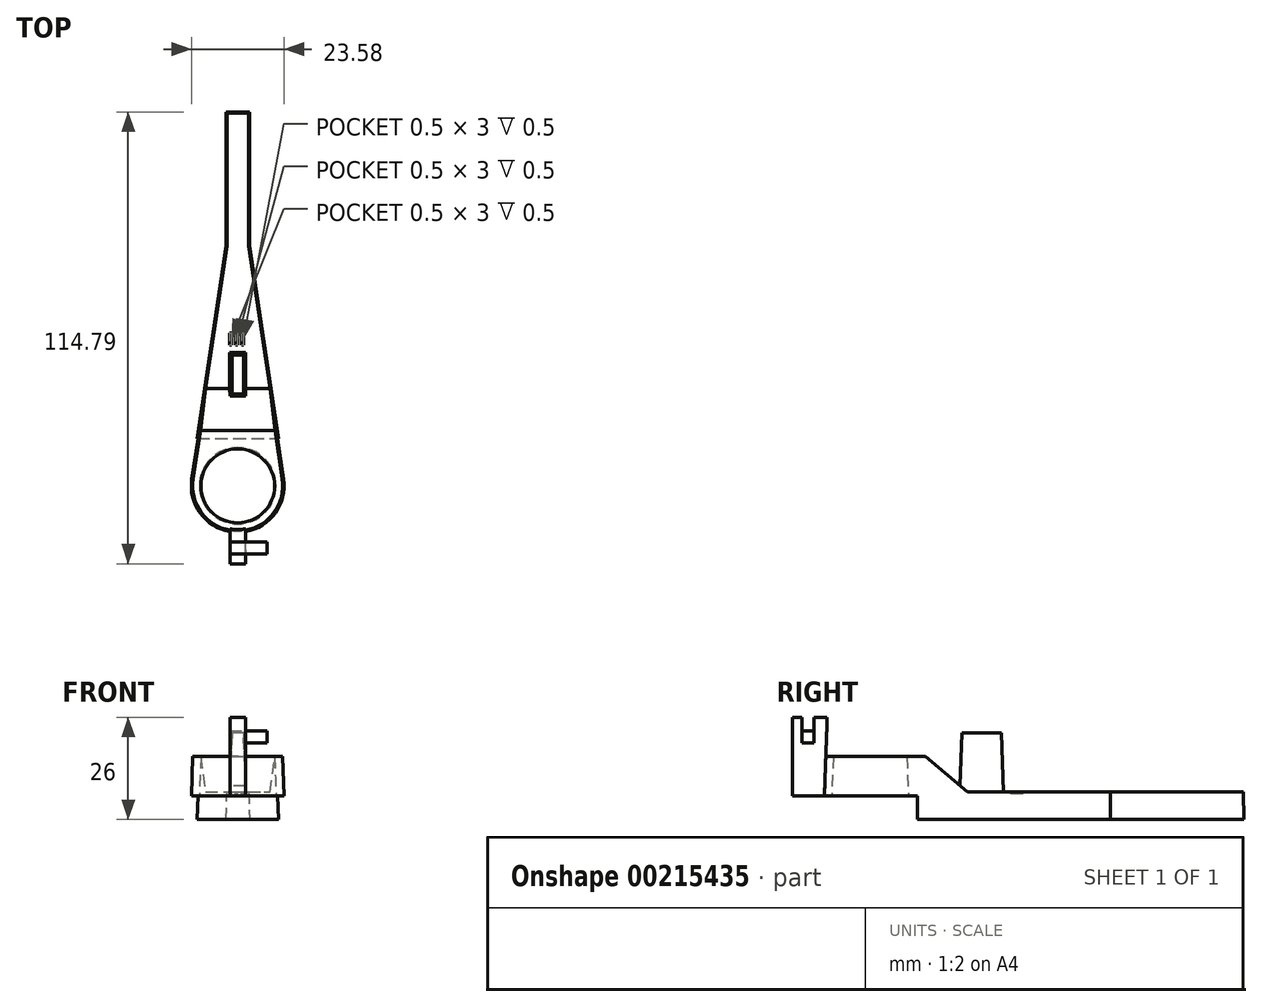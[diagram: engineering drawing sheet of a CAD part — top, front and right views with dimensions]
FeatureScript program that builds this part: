
annotation { "Feature Type Name" : "Feature", "Feature Type Description" : "" }
export const myFeature = defineFeature(function(context is Context, id is Id, definition is map)
    precondition{}
    {
        {
            var Q0;
            Q0=qCreatedBy(makeId("Top.planeOp"),FACE);
            var sketch = newSketch(context, id + "F0", { "sketchPlane" : qUnion([Q0])});
            skCircle(sketch, "E0", {"center": v(0, 0) * mm, "radius": 12 * mm});
            skLineSegment(sketch, "E1", {"start": v(-3, 95) * mm, "end": v(3, 95) * mm});
            skLineSegment(sketch, "E2", {"start": v(0, -12) * mm, "end": v(0, 95) * mm, "construction": true});
            skPoint(sketch, "E3", {"position": v(0, 95) * mm});
            skLineSegment(sketch, "E4", {"start": v(-3, 95) * mm, "end": v(-3, 61) * mm});
            skLineSegment(sketch, "E5", {"start": v(3, 95) * mm, "end": v(3, 61) * mm});
            skLineSegment(sketch, "E6", {"start": v(-3, 61) * mm, "end": v(-11.87, 1.78) * mm});
            skLineSegment(sketch, "E7", {"start": v(3, 61) * mm, "end": v(11.87, 1.78) * mm});
            skSolve(sketch);
        }
        {
            var Q0;
            Q0=qSketchRegion(id+"F0",true);
            extrude(context, id + "F1", {"entities" : qUnion([Q0]), "depth" : 16 * mm, "hasDraft" : true, "draftAngle" : 2 * degree, "draftPullDirection" : true});
        }
        {
            var Q0;
            Q0=qCreatedBy(makeId("Right.planeOp"),FACE);
            cPlane(context, id + "F2", {"entities" : qUnion([Q0]), "cplaneType" : CPlaneType.OFFSET, "offset" : 12 * mm, "width" : 150 * mm, "height" : 150 * mm});
        }
        {
            var Q0;
            Q0=qCreatedBy(id+"F2.planeOp",FACE);
            var sketch = newSketch(context, id + "F3", { "sketchPlane" : qUnion([Q0])});
            skLineSegment(sketch, "E8", {"start": v(94.76, 7) * mm, "end": v(24.76, 7) * mm});
            skLineSegment(sketch, "E9", {"start": v(24.76, 7) * mm, "end": v(14.03, 16) * mm});
            skLineSegment(sketch, "E10", {"start": v(12, 0) * mm, "end": v(12, 6) * mm});
            skLineSegment(sketch, "E11", {"start": v(12, 6) * mm, "end": v(-11.8, 6) * mm});
            skLineSegment(sketch, "E12", {"start": v(12, 0) * mm, "end": v(-12, 0) * mm});
            skLineSegment(sketch, "E13", {"start": v(-12, 0) * mm, "end": v(-11.8, 6) * mm});
            skLineSegment(sketch, "E14", {"start": v(14.03, 16) * mm, "end": v(94.44, 16) * mm});
            skLineSegment(sketch, "E15", {"start": v(94.44, 16) * mm, "end": v(94.76, 7) * mm});
            skSolve(sketch);
        }
        {
            var Q0;
            Q0=qSketchRegion(id+"F3",true);
            extrude(context, id + "F4", {"entities" : qUnion([Q0]), "operationType" : NewBodyOperationType.REMOVE, "endBound" : BoundingType.THROUGH_ALL, "oppositeDirection" : true, "depth" : 25 * mm});
        }
        {
            var Q0;
            Q0=makeQuery(id+"F4.boolean.opBoolean","COPY",FACE,{"derivedFrom":makeQuery(id+"F4.opExtrude","SWEPT_FACE",FACE,{"disambiguationData":[OSD([sQuery(id+"F3.wireOp",EDGE,"E8")])]})});
            cPlane(context, id + "F5", {"entities" : qUnion([Q0]), "cplaneType" : CPlaneType.OFFSET, "offset" : 15 * mm, "width" : 150 * mm, "height" : 150 * mm});
        }
        {
            var Q0;
            Q0=qCreatedBy(id+"F5.planeOp",FACE);
            var sketch = newSketch(context, id + "F6", { "sketchPlane" : qUnion([Q0])});
            skLineSegment(sketch, "E16.bottom", {"start": v(-1.5, 23.3) * mm, "end": v(1.5, 23.3) * mm});
            skLineSegment(sketch, "E16.top", {"start": v(-1.5, 33.3) * mm, "end": v(1.5, 33.3) * mm});
            skLineSegment(sketch, "E16.left", {"start": v(-1.5, 23.3) * mm, "end": v(-1.5, 33.3) * mm});
            skLineSegment(sketch, "E16.right", {"start": v(1.5, 23.3) * mm, "end": v(1.5, 33.3) * mm});
            skPoint(sketch, "E16.middle", {"position": v(0, 28.3) * mm});
            skSolve(sketch);
        }
        {
            var Q0;
            Q0=qSketchRegion(id+"F6",true);
            extrude(context, id + "F7", {"entities" : qUnion([Q0]), "operationType" : NewBodyOperationType.ADD, "endBound" : BoundingType.UP_TO_NEXT, "oppositeDirection" : true, "depth" : 25 * mm, "hasDraft" : true, "draftAngle" : 2 * degree});
        }
        {
            var Q0;
            Q0=makeQuery(id+"F4.boolean.opBoolean","COPY",FACE,{"derivedFrom":makeQuery(id+"F4.opExtrude","SWEPT_FACE",FACE,{"disambiguationData":[OSD([sQuery(id+"F3.wireOp",EDGE,"E11")])]})});
            var sketch = newSketch(context, id + "F8", { "sketchPlane" : qUnion([Q0])});
            skCircle(sketch, "E17", {"center": v(0, 0) * mm, "radius": 9.72 * mm});
            skSolve(sketch);
        }
        {
            var Q0;
            Q0=qSketchRegion(id+"F8",true);
            extrude(context, id + "F9", {"entities" : qUnion([Q0]), "operationType" : NewBodyOperationType.REMOVE, "endBound" : BoundingType.THROUGH_ALL, "oppositeDirection" : true, "depth" : 25 * mm, "hasDraft" : true, "draftAngle" : 2 * degree, "draftPullDirection" : true});
        }
        {
            var Q0;
            Q0=makeQuery(id+"F4.boolean.opBoolean","COPY",FACE,{"derivedFrom":makeQuery(id+"F4.opExtrude","SWEPT_FACE",FACE,{"disambiguationData":[OSD([sQuery(id+"F3.wireOp",EDGE,"E11")])]})});
            var sketch = newSketch(context, id + "F10", { "sketchPlane" : qUnion([Q0])});
            skLineSegment(sketch, "E18", {"start": v(0, 11.8) * mm, "end": v(0, 19.8) * mm, "construction": true});
            skPoint(sketch, "E18.endSnap0", {"position": v(0, 11.8) * mm});
            skLineSegment(sketch, "E19", {"start": v(0, 19.8) * mm, "end": v(-2, 19.8) * mm});
            skLineSegment(sketch, "E20", {"start": v(-2, 19.8) * mm, "end": v(-2, 11.62) * mm});
            skLineSegment(sketch, "E21", {"start": v(0, 19.8) * mm, "end": v(2, 19.8) * mm});
            skLineSegment(sketch, "E22", {"start": v(2, 19.8) * mm, "end": v(2, 11.62) * mm});
            skArc(sketch, "E23", {"start": v(2, 11.62) * mm, "mid": v(0, 11.8) * mm, "end": v(-2, 11.62) * mm});
            skSolve(sketch);
        }
        {
            var Q0;
            Q0=qCreatedBy(makeId("Front.planeOp"),FACE);
            var Q1;
            Q1=sQuery(id+"F10.wireOp",VERTEX,"E21.start");
            cPlane(context, id + "F11", {"entities" : qUnion([Q0, Q1]), "cplaneType" : CPlaneType.PLANE_POINT, "offset" : 25 * mm, "width" : 150 * mm, "height" : 150 * mm});
        }
        {
            var Q0;
            Q0=qCreatedBy(id+"F11.planeOp",FACE);
            var sketch = newSketch(context, id + "F12", { "sketchPlane" : qUnion([Q0])});
            skLineSegment(sketch, "E24.bottom", {"start": v(-2, 6) * mm, "end": v(2, 6) * mm});
            skLineSegment(sketch, "E24.top", {"start": v(-2, 26) * mm, "end": v(2, 26) * mm});
            skLineSegment(sketch, "E24.left", {"start": v(-2, 6) * mm, "end": v(-2, 26) * mm});
            skLineSegment(sketch, "E24.right", {"start": v(2, 6) * mm, "end": v(2, 26) * mm});
            skSolve(sketch);
        }
        {
            var Q0;
            Q0=qSketchRegion(id+"F12",true);
            var Q1;
            Q1=makeQuery(id+"F1.opExtrude","SWEPT_FACE",FACE,{"disambiguationData":[OSD([sQuery(id+"F0.wireOp",EDGE,"E0")])]});
            extrude(context, id + "F13", {"entities" : qUnion([Q0]), "operationType" : NewBodyOperationType.ADD, "endBound" : BoundingType.UP_TO_SURFACE, "oppositeDirection" : true, "endBoundEntityFace" : qUnion([Q1]), "depth" : 8 * mm});
        }
        {
            var Q0;
            Q0=makeQuery(id+"F13.opExtrude","SWEPT_FACE",FACE,{"disambiguationData":[OSD([sQuery(id+"F12.wireOp",EDGE,"E24.right")])]});
            var sketch = newSketch(context, id + "F14", { "sketchPlane" : qUnion([Q0])});
            skLineSegment(sketch, "E25.bottom", {"start": v(-17.3, 22.5) * mm, "end": v(-14.3, 22.5) * mm});
            skLineSegment(sketch, "E25.top", {"start": v(-17.3, 19.5) * mm, "end": v(-14.3, 19.5) * mm});
            skLineSegment(sketch, "E25.left", {"start": v(-17.3, 22.5) * mm, "end": v(-17.3, 19.5) * mm});
            skLineSegment(sketch, "E25.right", {"start": v(-14.3, 22.5) * mm, "end": v(-14.3, 19.5) * mm});
            skSolve(sketch);
        }
        {
            var Q0;
            Q0=qSketchRegion(id+"F14",true);
            extrude(context, id + "F15", {"entities" : qUnion([Q0]), "operationType" : NewBodyOperationType.ADD, "depth" : 5.5 * mm});
        }
        {
            var Q0;
            Q0=makeQuery(id+"F13.opExtrude","SWEPT_FACE",FACE,{"disambiguationData":[OSD([sQuery(id+"F12.wireOp",EDGE,"E24.right")])]});
            var sketch = newSketch(context, id + "F16", { "sketchPlane" : qUnion([Q0])});
            skLineSegment(sketch, "E26.bottom", {"start": v(-17.3, 22.5) * mm, "end": v(-14.3, 22.5) * mm});
            skLineSegment(sketch, "E26.top", {"start": v(-17.3, 26) * mm, "end": v(-14.3, 26) * mm});
            skLineSegment(sketch, "E26.left", {"start": v(-17.3, 22.5) * mm, "end": v(-17.3, 26) * mm});
            skLineSegment(sketch, "E26.right", {"start": v(-14.3, 22.5) * mm, "end": v(-14.3, 26) * mm});
            skSolve(sketch);
        }
        {
            var Q0;
            Q0=qSketchRegion(id+"F16",true);
            extrude(context, id + "F17", {"entities" : qUnion([Q0]), "operationType" : NewBodyOperationType.REMOVE, "endBound" : BoundingType.THROUGH_ALL, "oppositeDirection" : true, "depth" : 25 * mm});
        }
        {
            var Q0;
            Q0=makeQuery(id+"F4.boolean.opBoolean","COPY",FACE,{"derivedFrom":makeQuery(id+"F4.opExtrude","SWEPT_FACE",FACE,{"disambiguationData":[OSD([sQuery(id+"F3.wireOp",EDGE,"E8")])]})});
            var sketch = newSketch(context, id + "F18", { "sketchPlane" : qUnion([Q0])});
            skLineSegment(sketch, "E27.bottom", {"start": v(-2.02, 38.82) * mm, "end": v(1.48, 38.82) * mm});
            skLineSegment(sketch, "E27.top", {"start": v(-2.02, 35.82) * mm, "end": v(1.48, 35.82) * mm});
            skLineSegment(sketch, "E27.left", {"start": v(-2.02, 38.82) * mm, "end": v(-2.02, 35.82) * mm});
            skLineSegment(sketch, "E27.right", {"start": v(1.48, 38.82) * mm, "end": v(1.48, 35.82) * mm});
            skLineSegment(sketch, "E28", {"start": v(-1.52, 38.82) * mm, "end": v(-1.52, 35.82) * mm});
            skLineSegment(sketch, "E29", {"start": v(-0.5, 38.82) * mm, "end": v(-0.5, 35.82) * mm});
            skLineSegment(sketch, "E30", {"start": v(0, 38.82) * mm, "end": v(0, 35.82) * mm});
            skLineSegment(sketch, "E31", {"start": v(0.98, 38.82) * mm, "end": v(0.98, 35.82) * mm});
            skSolve(sketch);
        }
        {
            var Q0;
            {var subQ0=sQuery(id+"F18.wireOp",EDGE,"E27.left");Q0=makeQuery(id+"F18.imprint","IMPRINT",FACE,{"disambiguationData":[TD([[makeQuery(id+"F18.imprint","IMPRINT",EDGE,{"derivedFrom":subQ0}),1.0]])]});}
            var Q1;
            {var subQ0=sQuery(id+"F18.wireOp",EDGE,"E29");Q1=makeQuery(id+"F18.imprint","IMPRINT",FACE,{"disambiguationData":[TD([[makeQuery(id+"F18.imprint","IMPRINT",EDGE,{"derivedFrom":subQ0}),1.0]])]});}
            var Q2;
            {var subQ0=sQuery(id+"F18.wireOp",EDGE,"E27.right");Q2=makeQuery(id+"F18.imprint","IMPRINT",FACE,{"disambiguationData":[TD([[makeQuery(id+"F18.imprint","IMPRINT",EDGE,{"derivedFrom":subQ0}),-1.0]])]});}
            extrude(context, id + "F19", {"entities" : qUnion([Q0, Q1, Q2]), "operationType" : NewBodyOperationType.REMOVE, "oppositeDirection" : true, "depth" : 0.5 * mm});
        }
    });
